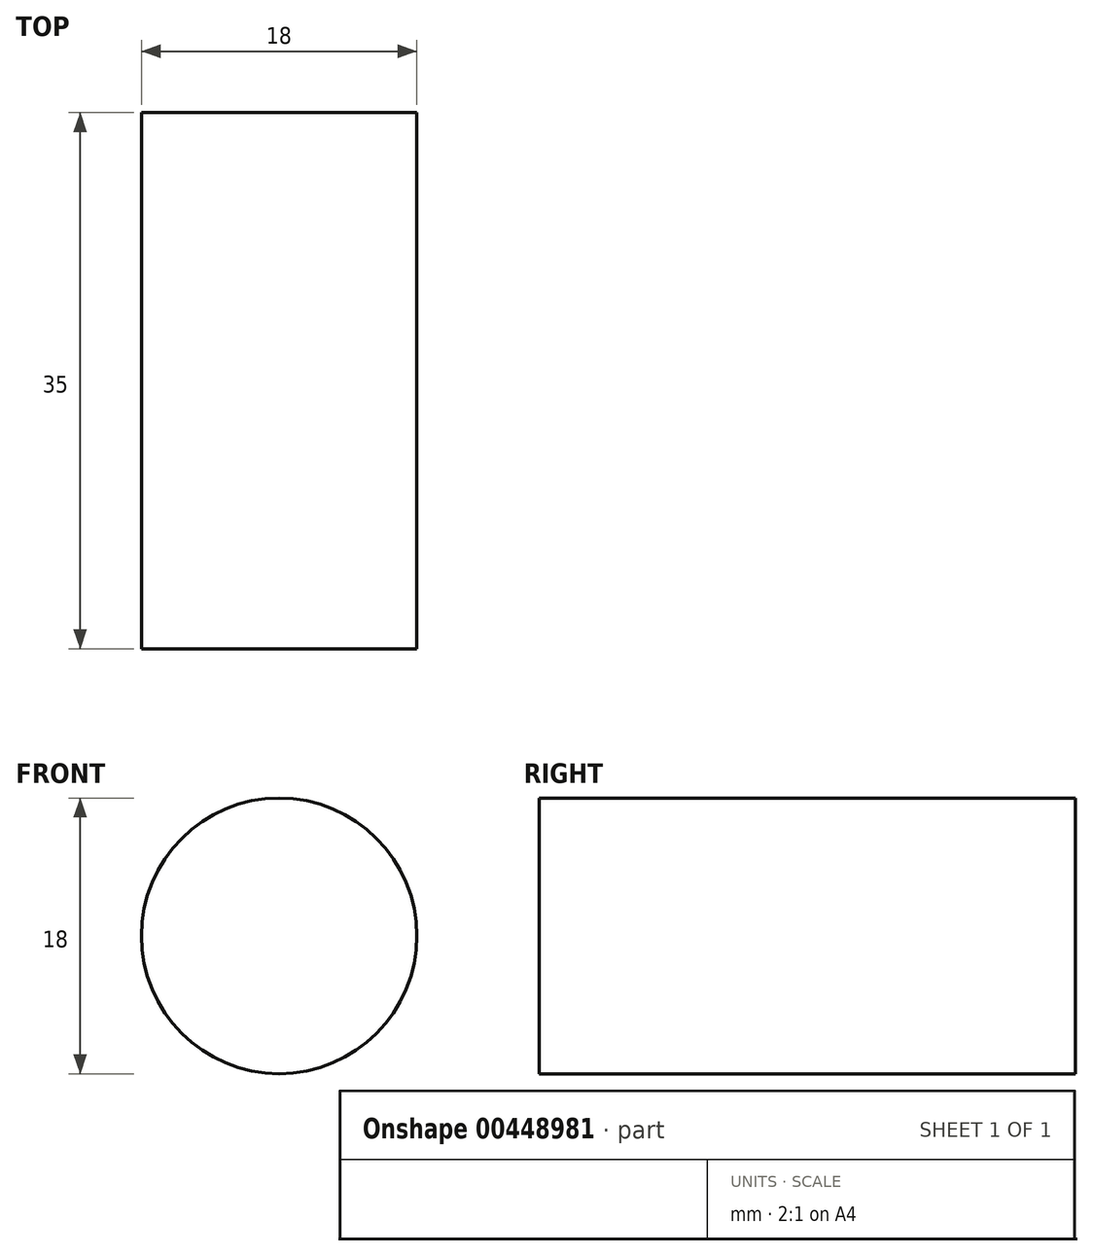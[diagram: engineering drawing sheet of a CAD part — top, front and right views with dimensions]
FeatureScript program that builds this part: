
annotation { "Feature Type Name" : "Feature", "Feature Type Description" : "" }
export const myFeature = defineFeature(function(context is Context, id is Id, definition is map)
    precondition{}
    {
        {
            var Q0;
            Q0=qCreatedBy(makeId("Front.planeOp"),FACE);
            var sketch = newSketch(context, id + "F0", { "sketchPlane" : qUnion([Q0])});
            skCircle(sketch, "E0", {"center": v(0, 0) * mm, "radius": 9 * mm});
            skSolve(sketch);
        }
        {
            var Q0;
            Q0 = qSketchRegion(id + "F0", true);
            extrude(context, id + "F1", {"entities" : qUnion([Q0]), "endBound" : BoundingType.SYMMETRIC, "depth" : 35 * mm, "offsetDistance" : 25 * mm});
        }
    });
